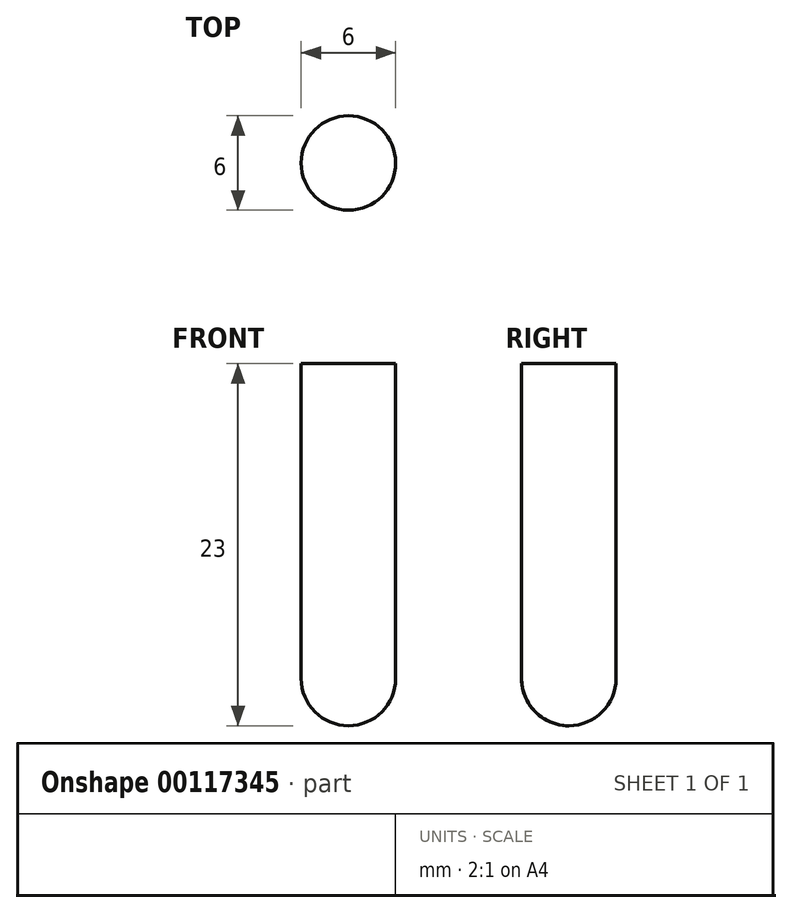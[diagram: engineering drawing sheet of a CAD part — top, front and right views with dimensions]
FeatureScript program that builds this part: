
annotation { "Feature Type Name" : "Feature", "Feature Type Description" : "" }
export const myFeature = defineFeature(function(context is Context, id is Id, definition is map)
    precondition{}
    {
        {
            var Q0;
            Q0=qCreatedBy(makeId("Top.planeOp"),FACE);
            var sketch = newSketch(context, id + "F0", { "sketchPlane" : qUnion([Q0])});
            skCircle(sketch, "E0", {"center": v(0, 0) * mm, "radius": 3 * mm});
            skSolve(sketch);
        }
        {
            var Q0;
            Q0 = qSketchRegion(id + "F0", true);
            extrude(context, id + "F1", {"entities" : qUnion([Q0]), "depth" : 20 * mm});
        }
        {
            var Q0;
            Q0=qCreatedBy(makeId("Right.planeOp"),FACE);
            var sketch = newSketch(context, id + "F2", { "sketchPlane" : qUnion([Q0])});
            skArc(sketch, "E1", {"start": v(-3, 0) * mm, "mid": v(-2.12, -2.12) * mm, "end": v(0, -3) * mm});
            skLineSegment(sketch, "E2", {"start": v(0, 0) * mm, "end": v(-3, 0) * mm});
            skLineSegment(sketch, "E3", {"start": v(0, 0) * mm, "end": v(0, -3) * mm});
            skLineSegment(sketch, "E4", {"start": v(0, 0) * mm, "end": v(0, -5.49) * mm});
            skSolve(sketch);
        }
        {
            var Q0;
            {var subQ0=sQuery(id+"F2.wireOp",EDGE,"E1");Q0=makeQuery(id+"F2.imprint","IMPRINT",FACE,{"disambiguationData":[TD([[makeQuery(id+"F2.imprint","IMPRINT",EDGE,{"derivedFrom":subQ0}),1.0]])]});}
            var Q1;
            Q1=sQuery(id+"F2.wireOp",EDGE,"E4");
            revolve(context, id + "F3", {"operationType" : NewBodyOperationType.ADD, "entities" : qUnion([Q0]), "axis" : qUnion([Q1]), "revolveType" : RevolveType.FULL});
        }
    });
